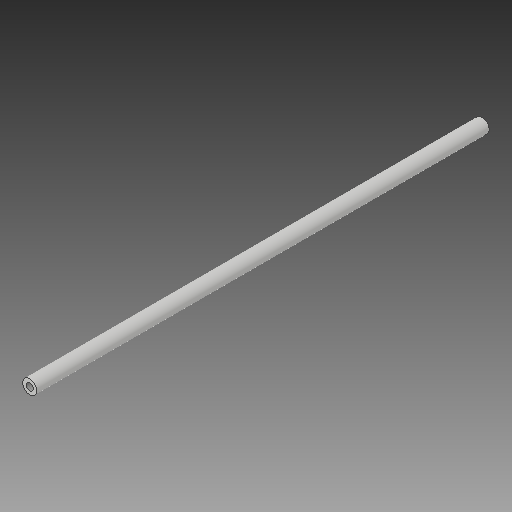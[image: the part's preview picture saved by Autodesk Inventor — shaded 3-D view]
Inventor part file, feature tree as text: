
AUTODESK INVENTOR PART (.ipt)
format: ipt  version: 2019 (Build 230136000, 136)  size: 99,840 bytes
history: native  units: in
note: dims shown in document units (in); Inventor stores cm internally (conversion verified against a paired STEP export)
features: sketch x2, extrude x1, hole x1, mirror x1
ambient origin geometry x8: Origin, YZ Plane, XZ Plane, XY Plane, X Axis, Y Axis, Z Axis, Center Point
bodies: Solid1 (feature_tree)
feature tree (5):
  extrude  "Extrusion1"  Depth=8.02in TaperAngle=0.0deg
  hole  "Hole1"  [1 undecoded]
  mirror  "Mirror1"
  sketch  "Sketch1"  dims[d0=0.25in d1=8.02in d2=0.0in]
  sketch  "Sketch2"  dims[d3=0.13in d4=0.328in d5=0.281in d6=0.138in d7=0.5635in d8=0.484in d9=0.8108in]
note: 1 required parameter value undecoded (feature->parameter linkage not recoverable at this tier; creation-order binding heuristic only, values carry confidence <= 0.55)
